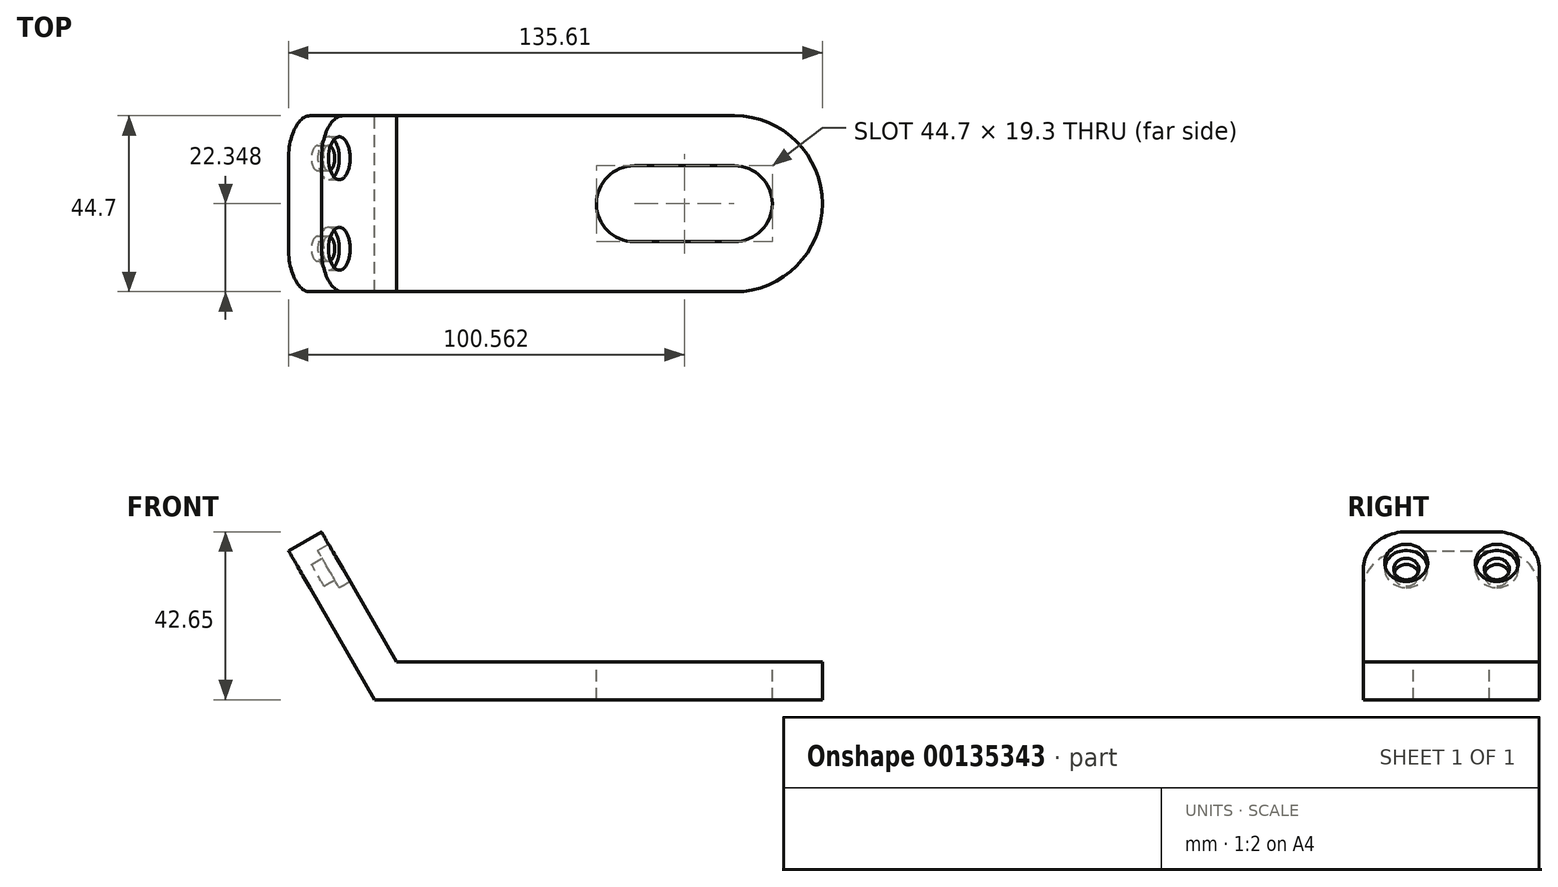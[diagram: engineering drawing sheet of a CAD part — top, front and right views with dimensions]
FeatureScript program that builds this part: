
annotation { "Feature Type Name" : "Feature", "Feature Type Description" : "" }
export const myFeature = defineFeature(function(context is Context, id is Id, definition is map)
    precondition{}
    {
        {
            var Q0;
            Q0=qCreatedBy(makeId("Front.planeOp"),FACE);
            var sketch = newSketch(context, id + "F0", { "sketchPlane" : qUnion([Q0])});
            skLineSegment(sketch, "E0", {"start": v(85.85, 0) * mm, "end": v(85.85, 9.65) * mm});
            skLineSegment(sketch, "E1", {"start": v(85.85, 9.65) * mm, "end": v(0, 9.65) * mm});
            skLineSegment(sketch, "E2", {"start": v(0, 9.65) * mm, "end": v(-19.05, 42.65) * mm});
            skLineSegment(sketch, "E3", {"start": v(-19.05, 42.65) * mm, "end": v(-27.4, 37.82) * mm});
            skLineSegment(sketch, "E4", {"start": v(-27.4, 37.82) * mm, "end": v(-5.57, 0) * mm});
            skLineSegment(sketch, "E5", {"start": v(-5.57, 0) * mm, "end": v(85.85, 0) * mm});
            skSolve(sketch);
        }
        {
            var Q0;
            Q0=makeQuery(id+"F0.imprint","IMPRINT",FACE,{"disambiguationData":[TD([[makeQuery(id+"F0.imprint","IMPRINT",EDGE,{"derivedFrom":sQuery(id+"F0.wireOp",EDGE,"E0")}),1.0]])]});
            extrude(context, id + "F1", {"entities" : qUnion([Q0]), "depth" : 44.7 * mm});
        }
        {
            var Q0;
            Q0=makeQuery(id+"F1.opExtrude","SWEPT_FACE",FACE,{"disambiguationData":[OSD([sQuery(id+"F0.wireOp",EDGE,"E1")])]});
            var sketch = newSketch(context, id + "F2", { "sketchPlane" : qUnion([Q0])});
            skCircle(sketch, "E6", {"center": v(85.85, -22.35) * mm, "radius": 9.65 * mm});
            skCircle(sketch, "E7", {"center": v(60.45, -22.35) * mm, "radius": 9.65 * mm});
            skLineSegment(sketch, "E8", {"start": v(60.45, -12.7) * mm, "end": v(85.85, -12.7) * mm});
            skLineSegment(sketch, "E9", {"start": v(60.45, -32) * mm, "end": v(85.85, -32) * mm});
            skArc(sketch, "E10", {"start": v(85.85, -44.7) * mm, "mid": v(108.2, -22.35) * mm, "end": v(85.85, 0) * mm});
            skSolve(sketch);
        }
        {
            var Q0;
            Q0=makeQuery(id+"F2.imprint","IMPRINT",FACE,{"disambiguationData":[TD([[makeQuery(id+"F2.imprint","IMPRINT",EDGE,{"derivedFrom":sQuery(id+"F2.wireOp",EDGE,"E10")}),1.0]])]});
            extrude(context, id + "F3", {"entities" : qUnion([Q0]), "operationType" : NewBodyOperationType.ADD, "oppositeDirection" : true, "depth" : 9.65 * mm});
        }
        {
            var Q0;
            Q0 = qSketchRegion(id + "F2", true);
            extrude(context, id + "F4", {"entities" : qUnion([Q0]), "operationType" : NewBodyOperationType.REMOVE, "oppositeDirection" : true, "depth" : 25.4 * mm});
        }
        {
            var Q0;
            Q0=makeQuery(id+"F1.opExtrude","CAP_EDGE",EDGE,{"disambiguationData":[OSD([sQuery(id+"F0.wireOp",EDGE,"E3")])],"isStart":false});
            var Q1;
            Q1=makeQuery(id+"F1.opExtrude","CAP_EDGE",EDGE,{"disambiguationData":[OSD([sQuery(id+"F0.wireOp",EDGE,"E3")])],"isStart":true});
            fillet(context, id + "F5", {"entities" : qUnion([Q0, Q1]), "radius" : 10.92 * mm, "tangentPropagation" : true, "allowEdgeOverflow" : false});
        }
        {
            var Q0;
            Q0=makeQuery(id+"F1.opExtrude","SWEPT_FACE",FACE,{"disambiguationData":[OSD([sQuery(id+"F0.wireOp",EDGE,"E2")])]});
            var sketch = newSketch(context, id + "F6", { "sketchPlane" : qUnion([Q0])});
            skCircle(sketch, "E11", {"center": v(-33.78, 37.37) * mm, "radius": 5.46 * mm});
            skCircle(sketch, "E12", {"center": v(-10.77, 37.37) * mm, "radius": 5.46 * mm});
            skCircle(sketch, "E13", {"center": v(-33.78, 37.37) * mm, "radius": 3.18 * mm});
            skCircle(sketch, "E14", {"center": v(-10.77, 37.37) * mm, "radius": 3.18 * mm});
            skSolve(sketch);
        }
        {
            var Q0;
            Q0=makeQuery(id+"F6.imprint","IMPRINT",FACE,{"disambiguationData":[TD([[makeQuery(id+"F6.imprint","IMPRINT",EDGE,{"derivedFrom":sQuery(id+"F6.wireOp",EDGE,"E11")}),1.0]])]});
            var Q1;
            Q1=makeQuery(id+"F6.imprint","IMPRINT",FACE,{"disambiguationData":[TD([[makeQuery(id+"F6.imprint","IMPRINT",EDGE,{"derivedFrom":sQuery(id+"F6.wireOp",EDGE,"E12")}),1.0]])]});
            extrude(context, id + "F7", {"entities" : qUnion([Q0, Q1]), "operationType" : NewBodyOperationType.REMOVE, "oppositeDirection" : true, "depth" : 3.17 * mm});
        }
        {
            var Q0;
            Q0=makeQuery(id+"F7.boolean.opBoolean","SPLIT",FACE,{"disambiguationData":[TD([makeQuery(id+"F7.opExtrude","SWEPT_FACE",FACE,{"disambiguationData":[OSD([sQuery(id+"F6.wireOp",EDGE,"E13")])]})])],"derivedFrom":makeQuery(id+"F1.opExtrude","SWEPT_FACE",FACE,{"disambiguationData":[OSD([sQuery(id+"F0.wireOp",EDGE,"E2")])]})});
            var Q1;
            Q1=makeQuery(id+"F7.boolean.opBoolean","SPLIT",FACE,{"disambiguationData":[TD([makeQuery(id+"F7.opExtrude","SWEPT_FACE",FACE,{"disambiguationData":[OSD([sQuery(id+"F6.wireOp",EDGE,"E14")])]})])],"derivedFrom":makeQuery(id+"F1.opExtrude","SWEPT_FACE",FACE,{"disambiguationData":[OSD([sQuery(id+"F0.wireOp",EDGE,"E2")])]})});
            extrude(context, id + "F8", {"entities" : qUnion([Q0, Q1]), "operationType" : NewBodyOperationType.REMOVE, "oppositeDirection" : true, "depth" : 6.35 * mm});
        }
    });
